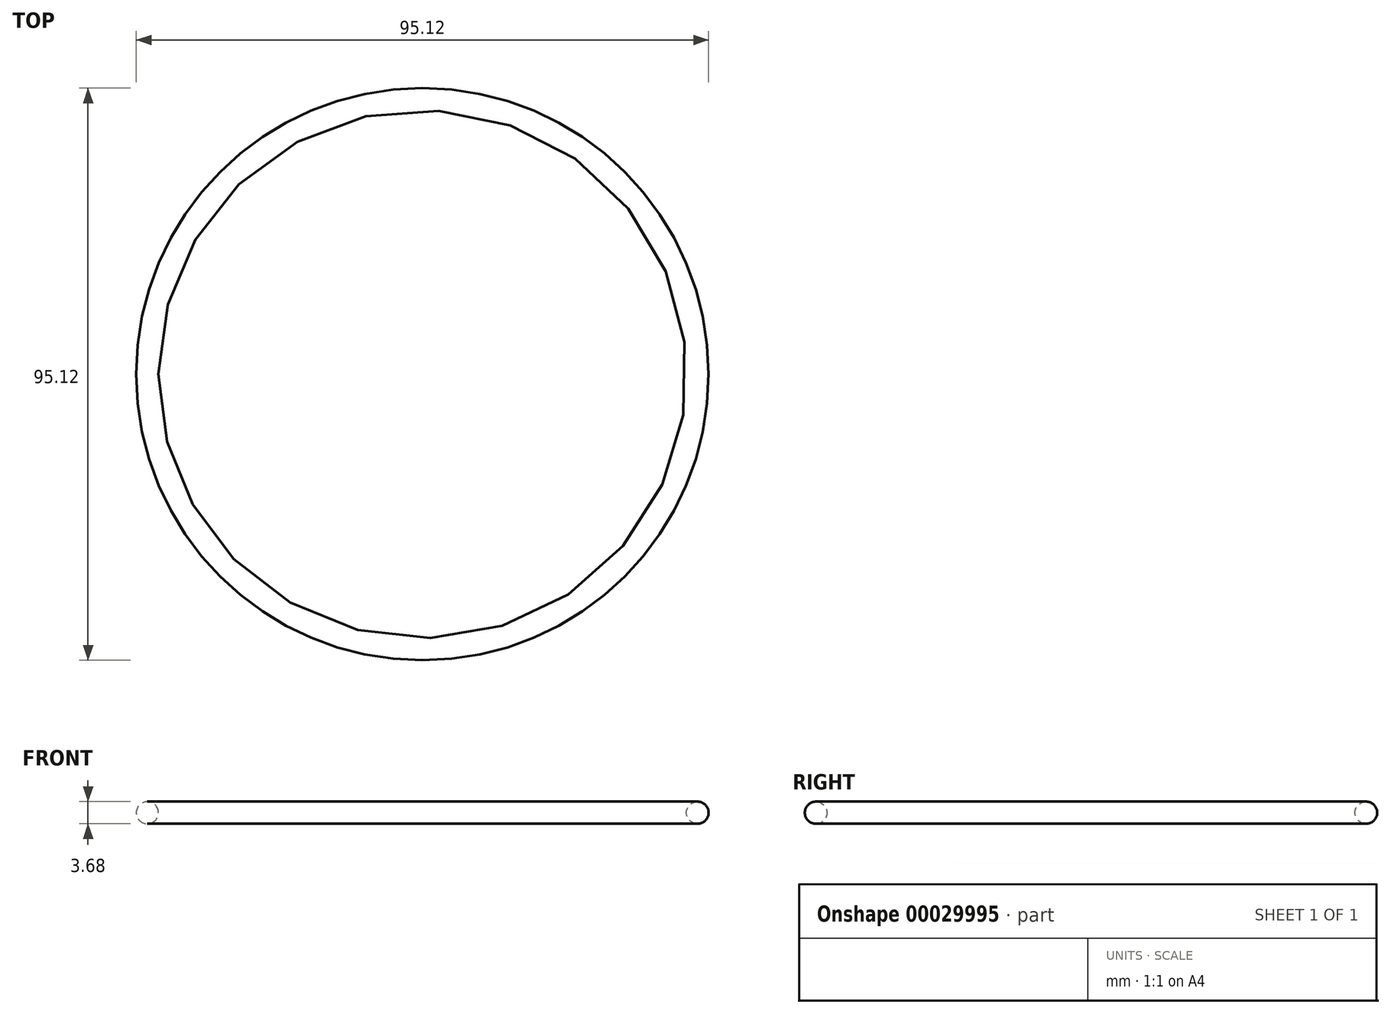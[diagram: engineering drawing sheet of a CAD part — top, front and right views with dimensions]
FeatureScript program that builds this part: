
annotation { "Feature Type Name" : "Feature", "Feature Type Description" : "" }
export const myFeature = defineFeature(function(context is Context, id is Id, definition is map)
    precondition{}
    {
        {
            var Q0;
            Q0=qCreatedBy(makeId("Front.planeOp"),FACE);
            var sketch = newSketch(context, id + "F0", { "sketchPlane" : qUnion([Q0])});
            skLineSegment(sketch, "E0", {"start": v(0, -70.54) * mm, "end": v(0, 121) * mm, "construction": true});
            skCircle(sketch, "E1", {"center": v(45.72, 0) * mm, "radius": 1.84 * mm});
            skSolve(sketch);
        }
        {
            var Q0;
            Q0=makeQuery(id+"F0.imprint","IMPRINT",FACE,{"disambiguationData":[TD([[makeQuery(id+"F0.imprint","IMPRINT",EDGE,{"derivedFrom":sQuery(id+"F0.wireOp",EDGE,"E1")}),1.0]])]});
            var Q1;
            Q1=sQuery(id+"F0.wireOp",EDGE,"E0");
            revolve(context, id + "F1", {"entities" : qUnion([Q0]), "axis" : qUnion([Q1]), "revolveType" : RevolveType.FULL});
        }
    });
